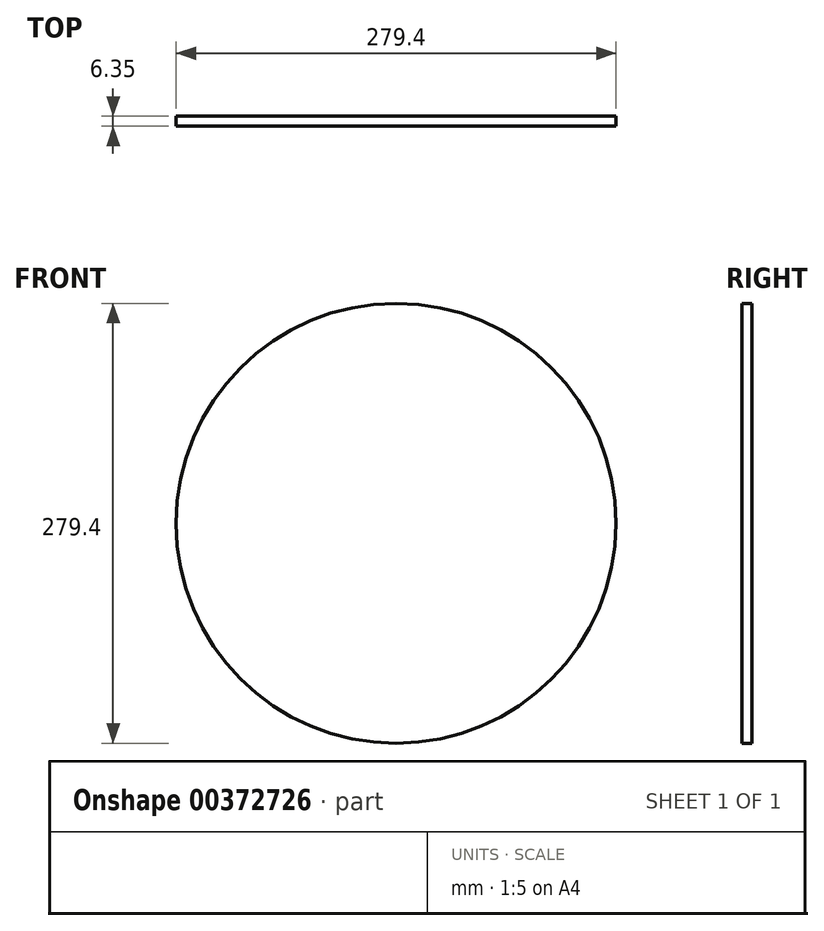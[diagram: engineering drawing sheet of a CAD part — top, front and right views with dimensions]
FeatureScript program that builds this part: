
annotation { "Feature Type Name" : "Feature", "Feature Type Description" : "" }
export const myFeature = defineFeature(function(context is Context, id is Id, definition is map)
    precondition{}
    {
        {
            var Q0;
            Q0=qCreatedBy(makeId("Front.planeOp"),FACE);
            var sketch = newSketch(context, id + "F0", { "sketchPlane" : qUnion([Q0])});
            skCircle(sketch, "E0", {"center": v(0, 0) * mm, "radius": 139.7 * mm});
            skSolve(sketch);
        }
        {
            var Q0;
            Q0 = qSketchRegion(id + "F0", true);
            extrude(context, id + "F1", {"entities" : qUnion([Q0]), "depth" : 6.35 * mm});
        }
    });
